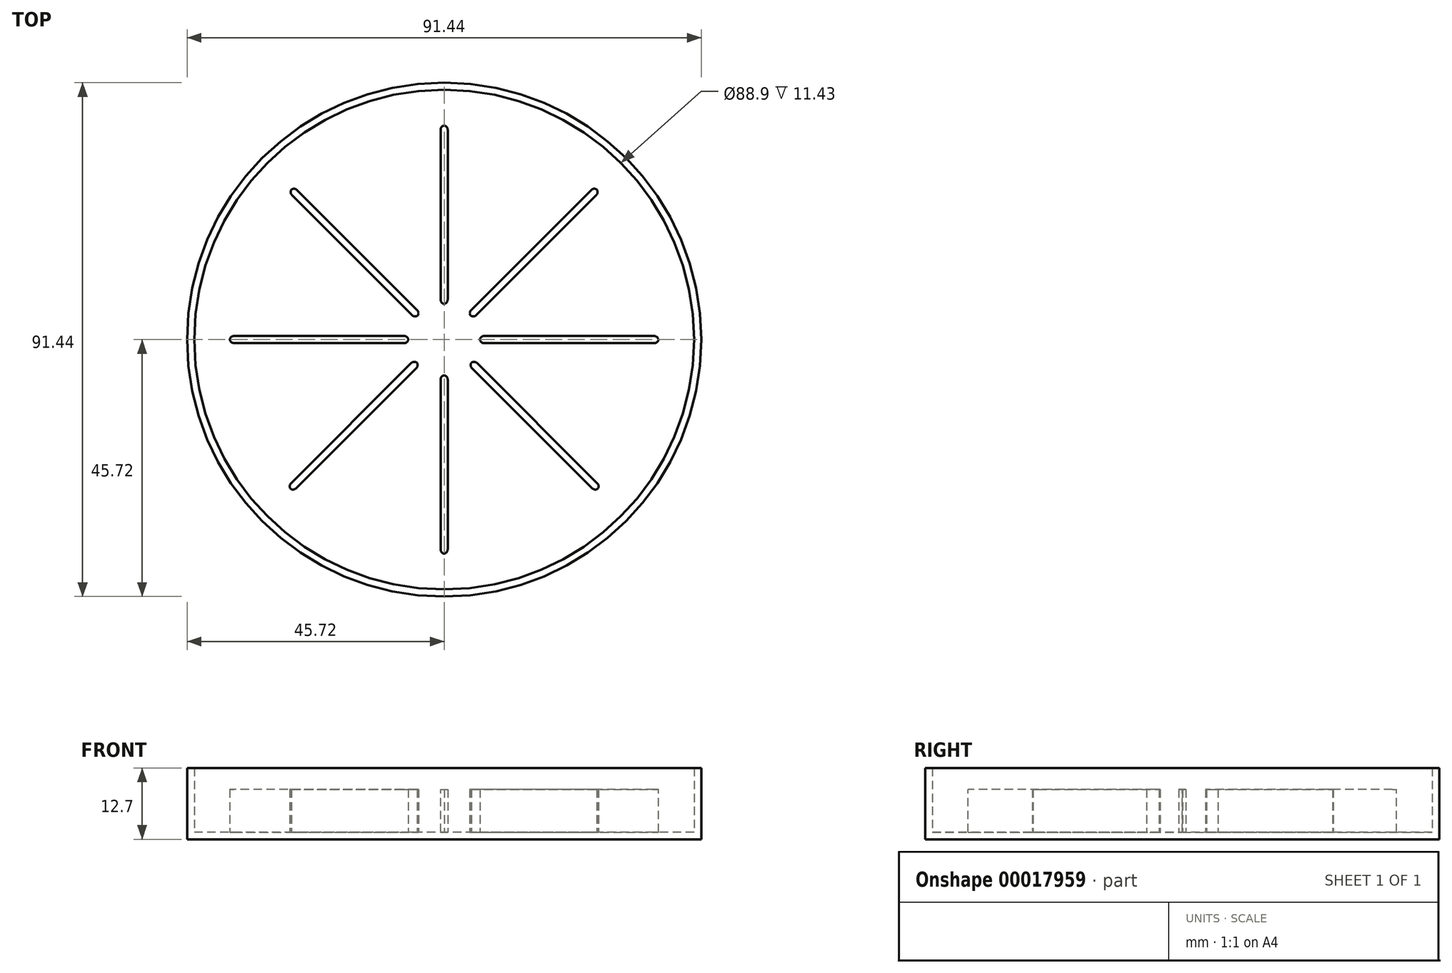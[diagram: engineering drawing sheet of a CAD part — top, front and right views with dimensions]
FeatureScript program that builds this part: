
annotation { "Feature Type Name" : "Feature", "Feature Type Description" : "" }
export const myFeature = defineFeature(function(context is Context, id is Id, definition is map)
    precondition{}
    {
        {
            var Q0;
            Q0=qCreatedBy(makeId("Top.planeOp"),FACE);
            var sketch = newSketch(context, id + "F0", { "sketchPlane" : qUnion([Q0])});
            skCircle(sketch, "E0", {"center": v(0, 0) * mm, "radius": 45.72 * mm});
            skSolve(sketch);
        }
        {
            var Q0;
            Q0=makeQuery(id+"F0.imprint","IMPRINT",FACE,{"disambiguationData":[TD([[makeQuery(id+"F0.imprint","IMPRINT",EDGE,{"derivedFrom":sQuery(id+"F0.wireOp",EDGE,"E0")}),1.0]])]});
            extrude(context, id + "F1", {"entities" : qUnion([Q0]), "depth" : 1.27 * mm, "offsetDistance" : 25.4 * mm});
        }
        {
            var Q0;
            Q0=makeQuery(id+"F1.opExtrude","CAP_FACE",FACE,{"disambiguationData":[OSD([sQuery(id+"F0.wireOp",EDGE,"E0")])],"isStart":false});
            var sketch = newSketch(context, id + "F2", { "sketchPlane" : qUnion([Q0])});
            skCircle(sketch, "E1", {"center": v(0, 0) * mm, "radius": 44.45 * mm});
            skSolve(sketch);
        }
        {
            var Q0;
            Q0=makeQuery(id+"F2.imprint","IMPRINT",FACE,{"disambiguationData":[TD([[makeQuery(id+"F2.imprint","IMPRINT",EDGE,{"derivedFrom":sQuery(id+"F2.wireOp",EDGE,"E1")}),-1.0]])]});
            extrude(context, id + "F3", {"entities" : qUnion([Q0]), "operationType" : NewBodyOperationType.ADD, "depth" : 11.43 * mm, "offsetDistance" : 25.4 * mm});
        }
        {
            var Q0;
            Q0=qCreatedBy(makeId("Top.planeOp"),FACE);
            var sketch = newSketch(context, id + "F4", { "sketchPlane" : qUnion([Q0])});
            skLineSegment(sketch, "E2", {"start": v(0, 0) * mm, "end": v(42, 42) * mm, "construction": true});
            skSolve(sketch);
        }
        {
            var Q0;
            Q0=qCreatedBy(makeId("Top.planeOp"),FACE);
            var sketch = newSketch(context, id + "F5", { "sketchPlane" : qUnion([Q0])});
            skLineSegment(sketch, "E3.bottom", {"start": v(38.1, -0.63) * mm, "end": v(6.32, -0.63) * mm});
            skLineSegment(sketch, "E3.left", {"start": v(38.1, -0.63) * mm, "end": v(38.15, 0.63) * mm});
            skLineSegment(sketch, "E3.right", {"start": v(-38.15, -0.63) * mm, "end": v(-38.1, 0.63) * mm});
            skPoint(sketch, "E3.middle", {"position": v(0, 0) * mm});
            skLineSegment(sketch, "E4.bottom", {"start": v(0.63, 38.1) * mm, "end": v(-0.64, 38.1) * mm});
            skLineSegment(sketch, "E4.top", {"start": v(0.64, -38.1) * mm, "end": v(-0.63, -38.1) * mm});
            skLineSegment(sketch, "E4.left", {"start": v(0.63, 34.39) * mm, "end": v(0.63, 6.32) * mm});
            skLineSegment(sketch, "E4.right", {"start": v(-0.64, 34.39) * mm, "end": v(-0.64, 6.32) * mm});
            skLineSegment(sketch, "E5", {"start": v(-27.61, 26.27) * mm, "end": v(-5.11, 3.77) * mm});
            skLineSegment(sketch, "E6", {"start": v(26.88, -27) * mm, "end": v(27.77, -26.1) * mm});
            skLineSegment(sketch, "E7", {"start": v(27.77, -26.1) * mm, "end": v(5.24, -3.58) * mm});
            skLineSegment(sketch, "E8", {"start": v(-26.72, 27.17) * mm, "end": v(-27.61, 26.27) * mm});
            skLineSegment(sketch, "E9.MirrorCS", {"start": v(26.72, 27.17) * mm, "end": v(27.61, 26.27) * mm});
            skLineSegment(sketch, "E10.MirrorCS", {"start": v(27.61, 26.27) * mm, "end": v(5.11, 3.77) * mm});
            skLineSegment(sketch, "E11.MirrorCS", {"start": v(-26.88, -27) * mm, "end": v(-27.77, -26.1) * mm});
            skLineSegment(sketch, "E12.MirrorCS", {"start": v(-27.77, -26.1) * mm, "end": v(-5.24, -3.58) * mm});
            skLineSegment(sketch, "E13.trimOffspring", {"start": v(-0.64, -6.32) * mm, "end": v(-0.63, -38.1) * mm});
            skLineSegment(sketch, "E14.trimOffspring", {"start": v(-6.32, 0.63) * mm, "end": v(-38.1, 0.63) * mm});
            skLineSegment(sketch, "E15.trimOffspring", {"start": v(0.63, -6.32) * mm, "end": v(0.64, -38.1) * mm});
            skLineSegment(sketch, "E16.trimOffspring", {"start": v(-6.32, -0.63) * mm, "end": v(-38.15, -0.63) * mm});
            skLineSegment(sketch, "E17", {"start": v(6.32, 0.63) * mm, "end": v(38.15, 0.63) * mm});
            skPoint(sketch, "E18.MirrorCS.end.orphan", {"position": v(-1.36, 2.7) * mm});
            skPoint(sketch, "E18.MirrorCS.start.orphan", {"position": v(-2.3, 0.63) * mm});
            skPoint(sketch, "E19.MirrorCS.end.orphan", {"position": v(1.36, 2.7) * mm});
            skPoint(sketch, "E19.MirrorCS.start.orphan", {"position": v(2.3, 0.63) * mm});
            skPoint(sketch, "E20.end.orphan", {"position": v(1.36, -2.7) * mm});
            skPoint(sketch, "E21.MirrorCS.end.orphan", {"position": v(-1.36, -2.7) * mm});
            skPoint(sketch, "E21.MirrorCS.start.orphan", {"position": v(-2.3, -0.63) * mm});
            skArc(sketch, "E22", {"start": v(0.63, 6.32) * mm, "mid": v(0, 6.35) * mm, "end": v(-0.64, 6.32) * mm});
            skLineSegment(sketch, "E23.trimOffspring", {"start": v(-4.26, 4.7) * mm, "end": v(-26.72, 27.17) * mm});
            skLineSegment(sketch, "E24.trimOffspring", {"start": v(4.26, 4.7) * mm, "end": v(26.72, 27.17) * mm});
            skPoint(sketch, "E25.orphan", {"position": v(2.3, -0.63) * mm});
            skLineSegment(sketch, "E26.trimOffspring", {"start": v(4.42, -4.56) * mm, "end": v(26.88, -27) * mm});
            skLineSegment(sketch, "E27.trimOffspring", {"start": v(-4.42, -4.56) * mm, "end": v(-26.88, -27) * mm});
            skArc(sketch, "E28.trimOffspring", {"start": v(-4.26, 4.7) * mm, "mid": v(-4.71, 4.26) * mm, "end": v(-5.11, 3.77) * mm});
            skArc(sketch, "E29.trimOffspring", {"start": v(-6.32, 0.63) * mm, "mid": v(-6.35, 0) * mm, "end": v(-6.32, -0.63) * mm});
            skArc(sketch, "E30.trimOffspring", {"start": v(-5.24, -3.58) * mm, "mid": v(-4.86, -4.09) * mm, "end": v(-4.42, -4.56) * mm});
            skArc(sketch, "E31.trimOffspring", {"start": v(-0.64, -6.32) * mm, "mid": v(0, -6.35) * mm, "end": v(0.63, -6.32) * mm});
            skArc(sketch, "E32.trimOffspring", {"start": v(4.42, -4.56) * mm, "mid": v(4.86, -4.09) * mm, "end": v(5.24, -3.58) * mm});
            skArc(sketch, "E33.trimOffspring", {"start": v(6.32, -0.63) * mm, "mid": v(6.35, 0) * mm, "end": v(6.32, 0.63) * mm});
            skArc(sketch, "E34.trimOffspring", {"start": v(5.11, 3.77) * mm, "mid": v(4.71, 4.26) * mm, "end": v(4.26, 4.7) * mm});
            skLineSegment(sketch, "E35", {"start": v(-0.64, 38.1) * mm, "end": v(-0.64, 34.39) * mm});
            skLineSegment(sketch, "E36", {"start": v(0.63, 38.1) * mm, "end": v(0.63, 34.39) * mm});
            skSolve(sketch);
        }
        {
            var Q0;
            Q0 = qSketchRegion(id + "F5", true);
            extrude(context, id + "F6", {"entities" : qUnion([Q0]), "operationType" : NewBodyOperationType.ADD, "depth" : 8.9 * mm, "offsetDistance" : 25.4 * mm});
        }
        {
            var Q0;
            Q0=makeQuery(id+"F6.opExtrude","SWEPT_EDGE",EDGE,{"disambiguationData":[OSD([sQuery(id+"F5.wireOp",EDGE,"E5"),sQuery(id+"F5.wireOp",EDGE,"E8")])]});
            var Q1;
            Q1=makeQuery(id+"F6.opExtrude","SWEPT_EDGE",EDGE,{"disambiguationData":[OSD([sQuery(id+"F5.wireOp",EDGE,"E4.bottom"),sQuery(id+"F5.wireOp",EDGE,"E4.right")])]});
            var Q2;
            Q2=makeQuery(id+"F6.opExtrude","SWEPT_EDGE",EDGE,{"disambiguationData":[OSD([sQuery(id+"F5.wireOp",EDGE,"E9.MirrorCS"),sQuery(id+"F5.wireOp",EDGE,"ea7f4763-9144-4597-b5ec-63135017ad59.trimOffspring")])]});
            var Q3;
            Q3=makeQuery(id+"F6.opExtrude","SWEPT_EDGE",EDGE,{"disambiguationData":[OSD([sQuery(id+"F5.wireOp",EDGE,"E3.right"),sQuery(id+"F5.wireOp",EDGE,"E16.trimOffspring")])]});
            var Q4;
            Q4=makeQuery(id+"F6.opExtrude","SWEPT_EDGE",EDGE,{"disambiguationData":[OSD([sQuery(id+"F5.wireOp",EDGE,"E11.MirrorCS"),sQuery(id+"F5.wireOp",EDGE,"b3050b6d-628a-48b0-ba69-332207cfbda7.trimOffspring")])]});
            var Q5;
            Q5=makeQuery(id+"F6.opExtrude","SWEPT_EDGE",EDGE,{"disambiguationData":[OSD([sQuery(id+"F5.wireOp",EDGE,"E4.top"),sQuery(id+"F5.wireOp",EDGE,"E13.trimOffspring")])]});
            var Q6;
            Q6=makeQuery(id+"F6.opExtrude","SWEPT_EDGE",EDGE,{"disambiguationData":[OSD([sQuery(id+"F5.wireOp",EDGE,"E6"),sQuery(id+"F5.wireOp",EDGE,"E7")])]});
            var Q7;
            Q7=makeQuery(id+"F6.opExtrude","SWEPT_EDGE",EDGE,{"disambiguationData":[OSD([sQuery(id+"F5.wireOp",EDGE,"E3.left"),sQuery(id+"F5.wireOp",EDGE,"E17")])]});
            var Q8;
            Q8=makeQuery(id+"F6.opExtrude","SWEPT_EDGE",EDGE,{"disambiguationData":[OSD([sQuery(id+"F5.wireOp",EDGE,"E11.MirrorCS"),sQuery(id+"F5.wireOp",EDGE,"E12.MirrorCS")])]});
            var Q9;
            Q9=makeQuery(id+"F6.opExtrude","SWEPT_EDGE",EDGE,{"disambiguationData":[OSD([sQuery(id+"F5.wireOp",EDGE,"E3.right"),sQuery(id+"F5.wireOp",EDGE,"E14.trimOffspring")])]});
            var Q10;
            Q10=makeQuery(id+"F6.opExtrude","SWEPT_EDGE",EDGE,{"disambiguationData":[OSD([sQuery(id+"F5.wireOp",EDGE,"E8"),sQuery(id+"F5.wireOp",EDGE,"5276f04b-f44e-447d-8aa3-511b9ebdaf47.trimOffspring")])]});
            var Q11;
            Q11=makeQuery(id+"F6.opExtrude","SWEPT_EDGE",EDGE,{"disambiguationData":[OSD([sQuery(id+"F5.wireOp",EDGE,"E4.top"),sQuery(id+"F5.wireOp",EDGE,"E15.trimOffspring")])]});
            var Q12;
            Q12=makeQuery(id+"F6.opExtrude","SWEPT_EDGE",EDGE,{"disambiguationData":[OSD([sQuery(id+"F5.wireOp",EDGE,"E6"),sQuery(id+"F5.wireOp",EDGE,"b3221db9-7350-4e05-bffc-c3ead4999e1a.trimOffspring")])]});
            var Q13;
            Q13=makeQuery(id+"F6.opExtrude","SWEPT_EDGE",EDGE,{"disambiguationData":[OSD([sQuery(id+"F5.wireOp",EDGE,"E3.bottom"),sQuery(id+"F5.wireOp",EDGE,"E3.left")])]});
            var Q14;
            Q14=makeQuery(id+"F6.opExtrude","SWEPT_EDGE",EDGE,{"disambiguationData":[OSD([sQuery(id+"F5.wireOp",EDGE,"E9.MirrorCS"),sQuery(id+"F5.wireOp",EDGE,"E10.MirrorCS")])]});
            var Q15;
            Q15=makeQuery(id+"F6.opExtrude","SWEPT_EDGE",EDGE,{"disambiguationData":[OSD([sQuery(id+"F5.wireOp",EDGE,"E4.bottom"),sQuery(id+"F5.wireOp",EDGE,"E4.left")])]});
            fillet(context, id + "F7", {"entities" : qUnion([Q0, Q1, Q2, Q3, Q4, Q5, Q6, Q7, Q8, Q9, Q10, Q11, Q12, Q13, Q14, Q15]), "radius" : 0.76 * mm, "tangentPropagation" : true, "allowEdgeOverflow" : false});
        }
        {
            var Q0;
            Q0=makeQuery(id+"F6.opExtrude","SWEPT_EDGE",EDGE,{"disambiguationData":[OSD([sQuery(id+"F5.wireOp",EDGE,"b3221db9-7350-4e05-bffc-c3ead4999e1a.trimOffspring"),sQuery(id+"F5.wireOp",EDGE,"E15.trimOffspring")])]});
            var Q1;
            Q1=makeQuery(id+"F6.opExtrude","SWEPT_EDGE",EDGE,{"disambiguationData":[OSD([sQuery(id+"F5.wireOp",EDGE,"E3.bottom"),sQuery(id+"F5.wireOp",EDGE,"E7")])]});
            var Q2;
            Q2=makeQuery(id+"F6.opExtrude","SWEPT_EDGE",EDGE,{"disambiguationData":[OSD([sQuery(id+"F5.wireOp",EDGE,"E10.MirrorCS"),sQuery(id+"F5.wireOp",EDGE,"E17")])]});
            var Q3;
            Q3=makeQuery(id+"F6.opExtrude","SWEPT_EDGE",EDGE,{"disambiguationData":[OSD([sQuery(id+"F5.wireOp",EDGE,"E4.left"),sQuery(id+"F5.wireOp",EDGE,"ea7f4763-9144-4597-b5ec-63135017ad59.trimOffspring")])]});
            var Q4;
            Q4=makeQuery(id+"F6.opExtrude","SWEPT_EDGE",EDGE,{"disambiguationData":[OSD([sQuery(id+"F5.wireOp",EDGE,"E4.right"),sQuery(id+"F5.wireOp",EDGE,"5276f04b-f44e-447d-8aa3-511b9ebdaf47.trimOffspring")])]});
            var Q5;
            Q5=makeQuery(id+"F6.opExtrude","SWEPT_EDGE",EDGE,{"disambiguationData":[OSD([sQuery(id+"F5.wireOp",EDGE,"E5"),sQuery(id+"F5.wireOp",EDGE,"E14.trimOffspring")])]});
            var Q6;
            Q6=makeQuery(id+"F6.opExtrude","SWEPT_EDGE",EDGE,{"disambiguationData":[OSD([sQuery(id+"F5.wireOp",EDGE,"E12.MirrorCS"),sQuery(id+"F5.wireOp",EDGE,"E16.trimOffspring")])]});
            var Q7;
            Q7=makeQuery(id+"F6.opExtrude","SWEPT_EDGE",EDGE,{"disambiguationData":[OSD([sQuery(id+"F5.wireOp",EDGE,"E13.trimOffspring"),sQuery(id+"F5.wireOp",EDGE,"b3050b6d-628a-48b0-ba69-332207cfbda7.trimOffspring")])]});
            var Q8;
            Q8=makeQuery(id+"F6.opExtrude","SWEPT_EDGE",EDGE,{"disambiguationData":[OSD([sQuery(id+"F5.wireOp",EDGE,"E23.trimOffspring"),sQuery(id+"F5.wireOp",EDGE,"E28.trimOffspring")])]});
            var Q9;
            Q9=makeQuery(id+"F6.opExtrude","SWEPT_EDGE",EDGE,{"disambiguationData":[OSD([sQuery(id+"F5.wireOp",EDGE,"E24.trimOffspring"),sQuery(id+"F5.wireOp",EDGE,"E34.trimOffspring")])]});
            var Q10;
            Q10=makeQuery(id+"F6.opExtrude","SWEPT_EDGE",EDGE,{"disambiguationData":[OSD([sQuery(id+"F5.wireOp",EDGE,"E26.trimOffspring"),sQuery(id+"F5.wireOp",EDGE,"E32.trimOffspring")])]});
            var Q11;
            Q11=makeQuery(id+"F6.opExtrude","SWEPT_EDGE",EDGE,{"disambiguationData":[OSD([sQuery(id+"F5.wireOp",EDGE,"E27.trimOffspring"),sQuery(id+"F5.wireOp",EDGE,"E30.trimOffspring")])]});
            fillet(context, id + "F8", {"entities" : qUnion([Q0, Q1, Q2, Q3, Q4, Q5, Q6, Q7, Q8, Q9, Q10, Q11]), "radius" : 0.76 * mm, "tangentPropagation" : true, "allowEdgeOverflow" : false});
        }
    });
